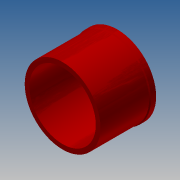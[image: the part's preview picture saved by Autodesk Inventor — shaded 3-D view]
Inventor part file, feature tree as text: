
AUTODESK INVENTOR PART (.ipt)
format: ipt  version: 2017.3 (Build 213257000, 257)  size: 117,760 bytes
history: native  units: in
note: dims shown in document units (in); Inventor stores cm internally (conversion verified against a paired STEP export)
features: other x3, extrude x2, sketch x2, chamfer x1
ambient origin geometry x8: Origin, YZ Plane, XZ Plane, XY Plane, X Axis, Y Axis, Z Axis, Center Point
bodies: Solid1 (feature_tree)
feature tree (8):
  other  "A1-19027-100-06 HCWI liner - pup.ipt"
  extrude  "Extrusion1"  Depth=0.5in TaperAngle=0.0deg
  extrude  "Extrusion2"  Depth=0.5in
  chamfer  "Chamfer1"  Distance=0.25in Angle=45.0deg
  other  "Solid1::A1-19027-100-06 HCWI liner - pup.ipt"
  other  "TaggingFeature1"
  sketch  "Sketch2"  dims[d0=0.3937in d1=0.5in d2=2.0in d3=0.0in d4=0.0in]
  sketch  "Sketch3"  dims[d5=0.5in d6=0.5in d7=0.0in d8=0.0in d9=0.25in d10=0.25in d11=0.125in d12=45.0deg]
